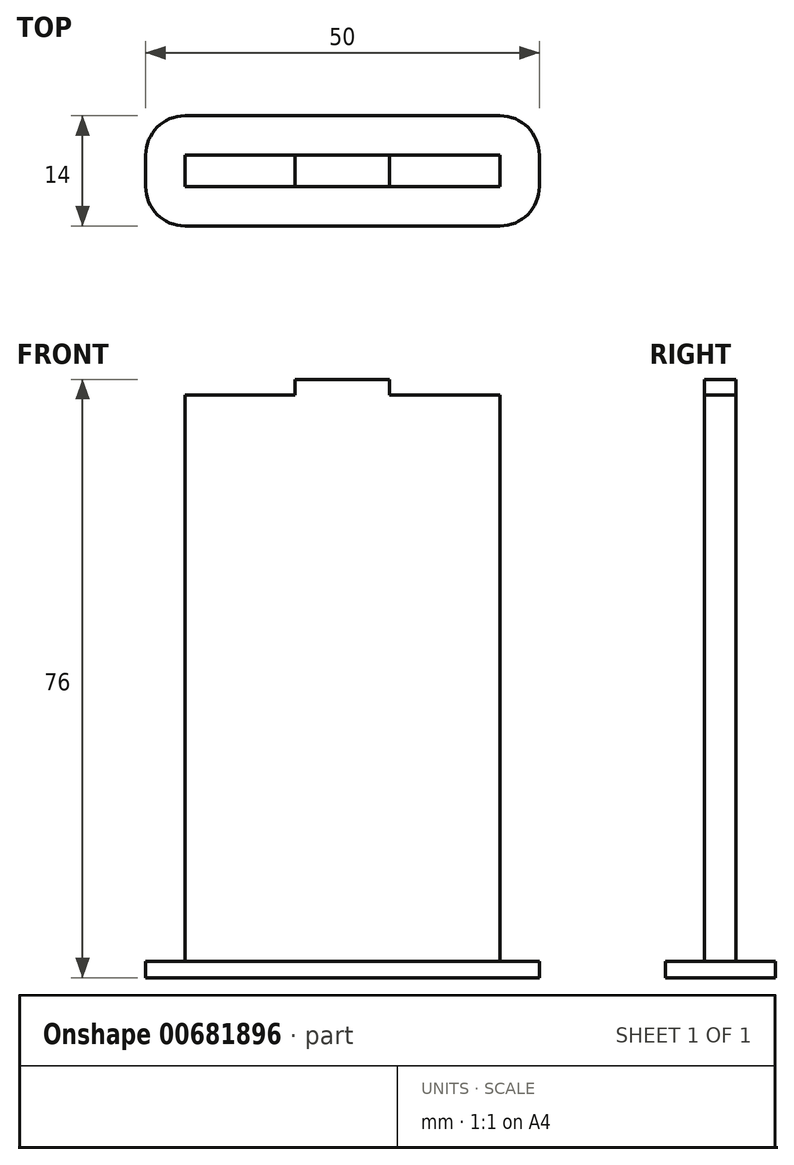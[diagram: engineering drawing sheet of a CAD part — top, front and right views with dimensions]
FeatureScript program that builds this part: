
annotation { "Feature Type Name" : "Feature", "Feature Type Description" : "" }
export const myFeature = defineFeature(function(context is Context, id is Id, definition is map)
    precondition{}
    {
        {
            assignVariable(context, id + "F0", {"name" : "a", "anyValue" : 4});
        }
        {
            var Q0;
            Q0=qCreatedBy(makeId("Front.planeOp"),FACE);
            var sketch = newSketch(context, id + "F1", { "sketchPlane" : qUnion([Q0])});
            skLineSegment(sketch, "E0.bottom", {"start": v(20, 0) * mm, "end": v(-20, 0) * mm});
            skLineSegment(sketch, "E0.top", {"start": v(20, 74) * mm, "end": v(6, 74) * mm});
            skLineSegment(sketch, "E0.left", {"start": v(20, 0) * mm, "end": v(20, 74) * mm});
            skLineSegment(sketch, "E0.right", {"start": v(-20, 0) * mm, "end": v(-20, 74) * mm});
            skLineSegment(sketch, "E1.top", {"start": v(6, 76) * mm, "end": v(-6, 76) * mm});
            skLineSegment(sketch, "E1.left", {"start": v(6, 74) * mm, "end": v(6, 76) * mm});
            skLineSegment(sketch, "E1.right", {"start": v(-6, 74) * mm, "end": v(-6, 76) * mm});
            skLineSegment(sketch, "E2.trimOffspring", {"start": v(-6, 74) * mm, "end": v(-20, 74) * mm});
            skPoint(sketch, "E3", {"position": v(0, 0) * mm});
            skPoint(sketch, "E4", {"position": v(0, 76) * mm});
            skSolve(sketch);
        }
        {
            var Q0;
            Q0 = qSketchRegion(id + "F1", true);
            extrude(context, id + "F2", {"entities" : qUnion([Q0]), "depth" : (getVariable(context, 'a')) * mm, "offsetDistance" : 25 * mm});
        }
        {
            var Q0;
            Q0=qCreatedBy(makeId("Top.planeOp"),FACE);
            var sketch = newSketch(context, id + "F3", { "sketchPlane" : qUnion([Q0])});
            skLineSegment(sketch, "E5.bottom", {"start": v(-25, 5) * mm, "end": v(25, 5) * mm});
            skLineSegment(sketch, "E5.top", {"start": v(-25, -9) * mm, "end": v(25, -9) * mm});
            skLineSegment(sketch, "E5.left", {"start": v(-25, 5) * mm, "end": v(-25, -9) * mm});
            skLineSegment(sketch, "E5.right", {"start": v(25, 5) * mm, "end": v(25, -9) * mm});
            skPoint(sketch, "E6", {"position": v(-25, -2) * mm});
            skPoint(sketch, "E7", {"position": v(0, 5) * mm});
            skLineSegment(sketch, "E8", {"start": v(-25, -2) * mm, "end": v(25, -2) * mm, "construction": true});
            skLineSegment(sketch, "E9", {"start": v(0, 5) * mm, "end": v(0, -9) * mm, "construction": true});
            skSolve(sketch);
        }
        {
            var Q0;
            Q0=makeQuery(id+"F3.imprint","IMPRINT",FACE,{"disambiguationData":[TD([[makeQuery(id+"F3.imprint","IMPRINT",EDGE,{"derivedFrom":sQuery(id+"F3.wireOp",EDGE,"E5.bottom")}),-1.0]])]});
            extrude(context, id + "F4", {"entities" : qUnion([Q0]), "operationType" : NewBodyOperationType.ADD, "depth" : 2.1 * mm, "offsetDistance" : 25 * mm});
        }
        {
            var Q0;
            Q0=makeQuery(id+"F4.opExtrude","SWEPT_EDGE",EDGE,{"disambiguationData":[OSD([sQuery(id+"F3.wireOp",EDGE,"E5.top"),sQuery(id+"F3.wireOp",EDGE,"E5.left")])]});
            var Q1;
            Q1=makeQuery(id+"F4.opExtrude","SWEPT_EDGE",EDGE,{"disambiguationData":[OSD([sQuery(id+"F3.wireOp",EDGE,"E5.top"),sQuery(id+"F3.wireOp",EDGE,"E5.right")])]});
            var Q2;
            Q2=makeQuery(id+"F4.opExtrude","SWEPT_EDGE",EDGE,{"disambiguationData":[OSD([sQuery(id+"F3.wireOp",EDGE,"E5.bottom"),sQuery(id+"F3.wireOp",EDGE,"E5.right")])]});
            var Q3;
            Q3=makeQuery(id+"F4.opExtrude","SWEPT_EDGE",EDGE,{"disambiguationData":[OSD([sQuery(id+"F3.wireOp",EDGE,"E5.bottom"),sQuery(id+"F3.wireOp",EDGE,"E5.left")])]});
            fillet(context, id + "F5", {"entities" : qUnion([Q0, Q1, Q2, Q3]), "radius" : 5 * mm, "tangentPropagation" : true, "allowEdgeOverflow" : false});
        }
    });
